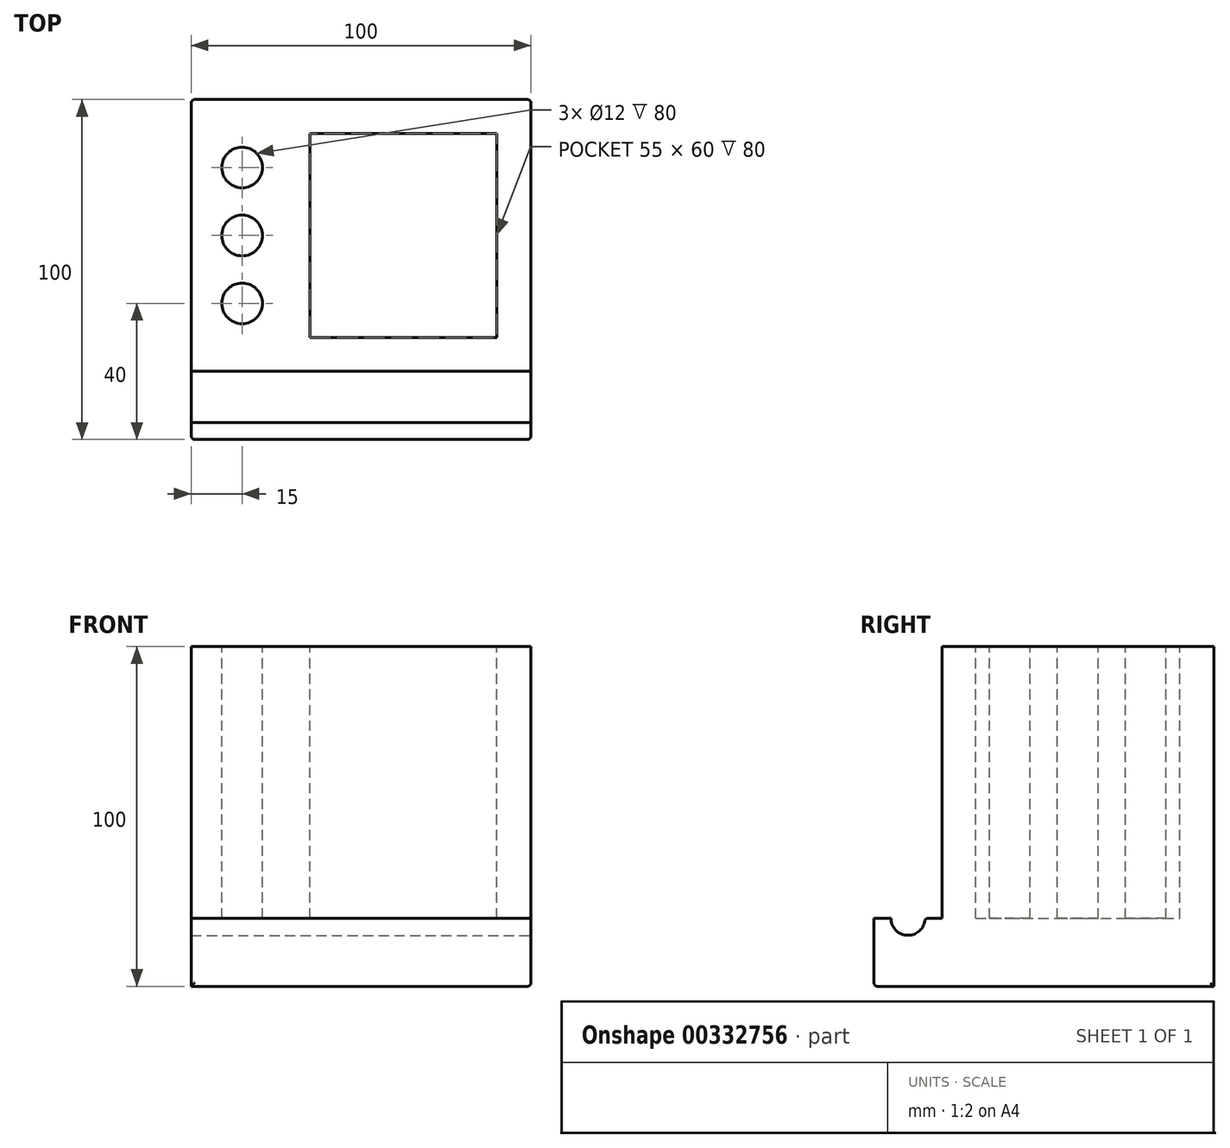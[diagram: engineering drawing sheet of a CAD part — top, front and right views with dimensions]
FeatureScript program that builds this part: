
annotation { "Feature Type Name" : "Feature", "Feature Type Description" : "" }
export const myFeature = defineFeature(function(context is Context, id is Id, definition is map)
    precondition{}
    {
        {
            var Q0;
            Q0=qCreatedBy(makeId("Top.planeOp"),FACE);
            var sketch = newSketch(context, id + "F0", { "sketchPlane" : qUnion([Q0])});
            skLineSegment(sketch, "E0.bottom", {"start": v(-50, 50) * mm, "end": v(50, 50) * mm});
            skLineSegment(sketch, "E0.top", {"start": v(-50, -50) * mm, "end": v(50, -50) * mm});
            skLineSegment(sketch, "E0.left", {"start": v(-50, 50) * mm, "end": v(-50, -50) * mm});
            skLineSegment(sketch, "E0.right", {"start": v(50, 50) * mm, "end": v(50, -50) * mm});
            skPoint(sketch, "E0.middle", {"position": v(0, 0) * mm});
            skSolve(sketch);
        }
        {
            var Q0;
            Q0 = qSketchRegion(id + "F0", true);
            extrude(context, id + "F1", {"entities" : qUnion([Q0]), "depth" : 100 * mm});
        }
        {
            var Q0;
            Q0=makeQuery(id+"F1.opExtrude","CAP_FACE",FACE,{"disambiguationData":[OSD([sQuery(id+"F0.wireOp",EDGE,"E0.bottom"),sQuery(id+"F0.wireOp",EDGE,"E0.top"),sQuery(id+"F0.wireOp",EDGE,"E0.left"),sQuery(id+"F0.wireOp",EDGE,"E0.right")])],"isStart":false});
            var sketch = newSketch(context, id + "F2", { "sketchPlane" : qUnion([Q0])});
            skLineSegment(sketch, "E1.bottom", {"start": v(-50, -30) * mm, "end": v(50, -30) * mm});
            skLineSegment(sketch, "E1.top", {"start": v(-50, -50) * mm, "end": v(50, -50) * mm});
            skLineSegment(sketch, "E1.left", {"start": v(-50, -30) * mm, "end": v(-50, -50) * mm});
            skLineSegment(sketch, "E1.right", {"start": v(50, -30) * mm, "end": v(50, -50) * mm});
            skPoint(sketch, "E1.middle", {"position": v(0, -40) * mm});
            skSolve(sketch);
        }
        {
            var Q0;
            Q0=makeQuery(id+"F2.imprint","IMPRINT",FACE,{"disambiguationData":[TD([[makeQuery(id+"F2.imprint","IMPRINT",EDGE,{"derivedFrom":sQuery(id+"F2.wireOp",EDGE,"E1.bottom")}),-1.0]])]});
            extrude(context, id + "F3", {"entities" : qUnion([Q0]), "operationType" : NewBodyOperationType.REMOVE, "oppositeDirection" : true, "depth" : 80 * mm});
        }
        {
            var Q0;
            Q0=makeQuery(id+"F1.opExtrude","CAP_FACE",FACE,{"disambiguationData":[OSD([sQuery(id+"F0.wireOp",EDGE,"E0.bottom"),sQuery(id+"F0.wireOp",EDGE,"E0.top"),sQuery(id+"F0.wireOp",EDGE,"E0.left"),sQuery(id+"F0.wireOp",EDGE,"E0.right")])],"isStart":false});
            var sketch = newSketch(context, id + "F4", { "sketchPlane" : qUnion([Q0])});
            skLineSegment(sketch, "E2.bottom", {"start": v(-15, 40) * mm, "end": v(40, 40) * mm});
            skLineSegment(sketch, "E2.top", {"start": v(-15, -20) * mm, "end": v(40, -20) * mm});
            skLineSegment(sketch, "E2.left", {"start": v(-15, 40) * mm, "end": v(-15, -20) * mm});
            skLineSegment(sketch, "E2.right", {"start": v(40, 40) * mm, "end": v(40, -20) * mm});
            skPoint(sketch, "E2.middle", {"position": v(12.5, 10) * mm});
            skLineSegment(sketch, "E3.bottom", {"start": v(-2.5, -20) * mm, "end": v(27.5, -20) * mm});
            skLineSegment(sketch, "E3.top", {"start": v(-2.5, -30) * mm, "end": v(27.5, -30) * mm});
            skLineSegment(sketch, "E3.left", {"start": v(-2.5, -20) * mm, "end": v(-2.5, -30) * mm});
            skLineSegment(sketch, "E3.right", {"start": v(27.5, -20) * mm, "end": v(27.5, -30) * mm});
            skPoint(sketch, "E3.middle", {"position": v(12.5, -25) * mm});
            skSolve(sketch);
        }
        {
            var Q0;
            Q0=makeQuery(id+"F4.imprint","IMPRINT",FACE,{"disambiguationData":[TD([[makeQuery(id+"F4.imprint","IMPRINT",EDGE,{"derivedFrom":sQuery(id+"F4.wireOp",EDGE,"E2.bottom")}),-1.0]])]});
            var Q1;
            Q1=makeQuery(id+"F4.imprint","IMPRINT",FACE,{"disambiguationData":[TD([[makeQuery(id+"F4.imprint","IMPRINT",EDGE,{"derivedFrom":sQuery(id+"F4.wireOp",EDGE,"E3.bottom")}),-1.0]])]});
            var Q2;
            Q2=makeQuery(id+"F3.boolean.opBoolean","COPY",FACE,{"derivedFrom":makeQuery(id+"F3.opExtrude","CAP_FACE",FACE,{"disambiguationData":[OSD([sQuery(id+"F2.wireOp",EDGE,"E1.bottom"),sQuery(id+"F2.wireOp",EDGE,"E1.top"),sQuery(id+"F2.wireOp",EDGE,"E1.left"),sQuery(id+"F2.wireOp",EDGE,"E1.right")])],"isStart":false})});
            extrude(context, id + "F5", {"entities" : qUnion([Q0, Q1]), "operationType" : NewBodyOperationType.REMOVE, "endBound" : BoundingType.UP_TO_SURFACE, "oppositeDirection" : true, "endBoundEntityFace" : qUnion([Q2]), "depth" : 25 * mm});
        }
        {
            var Q0;
            Q0=makeQuery(id+"F1.opExtrude","CAP_FACE",FACE,{"disambiguationData":[OSD([sQuery(id+"F0.wireOp",EDGE,"E0.bottom"),sQuery(id+"F0.wireOp",EDGE,"E0.top"),sQuery(id+"F0.wireOp",EDGE,"E0.left"),sQuery(id+"F0.wireOp",EDGE,"E0.right")])],"isStart":false});
            var sketch = newSketch(context, id + "F6", { "sketchPlane" : qUnion([Q0])});
            skCircle(sketch, "E4", {"center": v(-35, 30) * mm, "radius": 6 * mm});
            skCircle(sketch, "E5", {"center": v(-35, 10) * mm, "radius": 6 * mm});
            skCircle(sketch, "E6", {"center": v(-35, -10) * mm, "radius": 6 * mm});
            skLineSegment(sketch, "E7", {"start": v(-35, 10) * mm, "end": v(-35, 30) * mm, "construction": true});
            skLineSegment(sketch, "E8", {"start": v(-35, -10) * mm, "end": v(-35, 10) * mm, "construction": true});
            skLineSegment(sketch, "E9", {"start": v(-35, 30) * mm, "end": v(-35, 50) * mm, "construction": true});
            skLineSegment(sketch, "E10", {"start": v(-35, -10) * mm, "end": v(-35, -30) * mm, "construction": true});
            skSolve(sketch);
        }
        {
            var Q0;
            Q0=makeQuery(id+"F6.imprint","IMPRINT",FACE,{"disambiguationData":[TD([[makeQuery(id+"F6.imprint","IMPRINT",EDGE,{"derivedFrom":sQuery(id+"F6.wireOp",EDGE,"E6")}),1.0]])]});
            var Q1;
            Q1=makeQuery(id+"F6.imprint","IMPRINT",FACE,{"disambiguationData":[TD([[makeQuery(id+"F6.imprint","IMPRINT",EDGE,{"derivedFrom":sQuery(id+"F6.wireOp",EDGE,"E5")}),1.0]])]});
            var Q2;
            Q2=makeQuery(id+"F6.imprint","IMPRINT",FACE,{"disambiguationData":[TD([[makeQuery(id+"F6.imprint","IMPRINT",EDGE,{"derivedFrom":sQuery(id+"F6.wireOp",EDGE,"E4")}),1.0]])]});
            var Q3;
            Q3=makeQuery(id+"F5.boolean.opBoolean","MERGE",FACE,{"derivedFrom":[makeQuery(id+"F3.boolean.opBoolean","COPY",FACE,{"derivedFrom":makeQuery(id+"F3.opExtrude","CAP_FACE",FACE,{"disambiguationData":[OSD([sQuery(id+"F2.wireOp",EDGE,"E1.bottom"),sQuery(id+"F2.wireOp",EDGE,"E1.top"),sQuery(id+"F2.wireOp",EDGE,"E1.left"),sQuery(id+"F2.wireOp",EDGE,"E1.right")])],"isStart":false})})],"fromTools":[makeQuery(id+"F5.opExtrude","CAP_FACE",FACE,{"disambiguationData":[OSD([sQuery(id+"F4.wireOp",EDGE,"E2.bottom"),sQuery(id+"F4.wireOp",EDGE,"E2.top"),sQuery(id+"F4.wireOp",EDGE,"E2.left"),sQuery(id+"F4.wireOp",EDGE,"E2.right"),sQuery(id+"F4.wireOp",EDGE,"E3.top"),sQuery(id+"F4.wireOp",EDGE,"E3.left"),sQuery(id+"F4.wireOp",EDGE,"E3.right")])],"isStart":false})]});
            var Q4;
            Q4=makeQuery(id+"F1.opExtrude","SWEPT_BODY",BODY,{"disambiguationData":[OSD([sQuery(id+"F0.wireOp",EDGE,"E0.bottom"),sQuery(id+"F0.wireOp",EDGE,"E0.top"),sQuery(id+"F0.wireOp",EDGE,"E0.left"),sQuery(id+"F0.wireOp",EDGE,"E0.right")])]});
            extrude(context, id + "F7", {"entities" : qUnion([Q0, Q1, Q2]), "operationType" : NewBodyOperationType.REMOVE, "endBound" : BoundingType.UP_TO_SURFACE, "oppositeDirection" : true, "endBoundEntityFace" : qUnion([Q3]), "endBoundEntityBody" : qUnion([Q4]), "depth" : 25 * mm});
        }
        {
            var Q0;
            Q0=makeQuery(id+"F1.opExtrude","SWEPT_FACE",FACE,{"disambiguationData":[OSD([sQuery(id+"F0.wireOp",EDGE,"E0.right")])]});
            var sketch = newSketch(context, id + "F8", { "sketchPlane" : qUnion([Q0])});
            skCircle(sketch, "E11", {"center": v(-40, 20) * mm, "radius": 5 * mm});
            skSolve(sketch);
        }
        {
            var Q0;
            {var subQ0=sQuery(id+"F8.wireOp",EDGE,"E11");var subQ1=makeQuery(id+"F3.boolean.opBoolean","COPY",EDGE,{"derivedFrom":makeQuery(id+"F3.opExtrude","CAP_EDGE",EDGE,{"disambiguationData":[OSD([sQuery(id+"F2.wireOp",EDGE,"E1.right")])],"isStart":false})});var subQ2=makeQuery(id+"F8.imprint","INTERSECT",VERTEX,{"disambiguationData":[OD(0.0)],"derivedFrom":[subQ1,subQ0]});Q0=makeQuery(id+"F8.imprint","IMPRINT",FACE,{"disambiguationData":[TD([[makeQuery(id+"F8.imprint","IMPRINT",EDGE,{"disambiguationData":[TD([[subQ2,-1.0]])],"derivedFrom":subQ0}),1.0]])]});}
            var Q1;
            Q1=makeQuery(id+"F1.opExtrude","SWEPT_FACE",FACE,{"disambiguationData":[OSD([sQuery(id+"F0.wireOp",EDGE,"E0.left")])]});
            extrude(context, id + "F9", {"entities" : qUnion([Q0]), "operationType" : NewBodyOperationType.REMOVE, "endBound" : BoundingType.UP_TO_SURFACE, "oppositeDirection" : true, "endBoundEntityFace" : qUnion([Q1]), "depth" : 25 * mm});
        }
        {
            var Q0;
            {var subQ0=sQuery(id+"F8.wireOp",EDGE,"E11");var subQ1=sQuery(id+"F2.wireOp",EDGE,"E1.right");Q0=makeQuery(id+"F9.boolean.opBoolean","COPY",EDGE,{"derivedFrom":makeQuery(id+"F9.opExtrude","SWEPT_EDGE",EDGE,{"disambiguationData":[OSD([subQ1,subQ0]),TDD([makeQuery(id+"F8.imprint","INTERSECT",VERTEX,{"disambiguationData":[OD(1.0)],"derivedFrom":[makeQuery(id+"F3.boolean.opBoolean","COPY",EDGE,{"derivedFrom":makeQuery(id+"F3.opExtrude","CAP_EDGE",EDGE,{"disambiguationData":[OSD([subQ1])],"isStart":false})}),subQ0]})])]})});}
            var Q1;
            {var subQ0=sQuery(id+"F8.wireOp",EDGE,"E11");var subQ1=sQuery(id+"F2.wireOp",EDGE,"E1.right");Q1=makeQuery(id+"F9.boolean.opBoolean","COPY",EDGE,{"derivedFrom":makeQuery(id+"F9.opExtrude","SWEPT_EDGE",EDGE,{"disambiguationData":[OSD([subQ1,subQ0]),TDD([makeQuery(id+"F8.imprint","INTERSECT",VERTEX,{"disambiguationData":[OD(0.0)],"derivedFrom":[makeQuery(id+"F3.boolean.opBoolean","COPY",EDGE,{"derivedFrom":makeQuery(id+"F3.opExtrude","CAP_EDGE",EDGE,{"disambiguationData":[OSD([subQ1])],"isStart":false})}),subQ0]})])]})});}
            var Q2;
            Q2=makeQuery(id+"F1.opExtrude","SWEPT_EDGE",EDGE,{"disambiguationData":[OSD([sQuery(id+"F0.wireOp",EDGE,"E0.top"),sQuery(id+"F0.wireOp",EDGE,"E0.right")])]});
            var Q3;
            Q3=makeQuery(id+"F3.boolean.opBoolean","COPY",EDGE,{"derivedFrom":makeQuery(id+"F3.opExtrude","CAP_EDGE",EDGE,{"disambiguationData":[OSD([sQuery(id+"F2.wireOp",EDGE,"E1.top")])],"isStart":false})});
            var Q4;
            Q4=makeQuery(id+"F1.opExtrude","SWEPT_EDGE",EDGE,{"disambiguationData":[OSD([sQuery(id+"F0.wireOp",EDGE,"E0.top"),sQuery(id+"F0.wireOp",EDGE,"E0.left")])]});
            var Q5;
            Q5=makeQuery(id+"F1.opExtrude","CAP_EDGE",EDGE,{"disambiguationData":[OSD([sQuery(id+"F0.wireOp",EDGE,"E0.top")])],"isStart":true});
            var Q6;
            Q6=makeQuery(id+"F1.opExtrude","CAP_EDGE",EDGE,{"disambiguationData":[OSD([sQuery(id+"F0.wireOp",EDGE,"E0.right")])],"isStart":true});
            var Q7;
            Q7=makeQuery(id+"F9.boolean.opBoolean","COPY",EDGE,{"derivedFrom":makeQuery(id+"F9.opExtrude","CAP_EDGE",EDGE,{"disambiguationData":[OSD([sQuery(id+"F8.wireOp",EDGE,"E11")])],"isStart":true})});
            var Q8;
            {var subQ0=sQuery(id+"F2.wireOp",EDGE,"E1.right");Q8=makeQuery(id+"F9.boolean.opBoolean","SPLIT",EDGE,{"disambiguationData":[TD([makeQuery(id+"F1.opExtrude","SWEPT_FACE",FACE,{"disambiguationData":[OSD([sQuery(id+"F0.wireOp",EDGE,"E0.top")])]})])],"derivedFrom":makeQuery(id+"F3.boolean.opBoolean","COPY",EDGE,{"derivedFrom":makeQuery(id+"F3.opExtrude","CAP_EDGE",EDGE,{"disambiguationData":[OSD([subQ0])],"isStart":false})})});}
            var Q9;
            {var subQ0=sQuery(id+"F2.wireOp",EDGE,"E1.right");var subQ1=sQuery(id+"F2.wireOp",EDGE,"E1.bottom");Q9=makeQuery(id+"F9.boolean.opBoolean","SPLIT",EDGE,{"disambiguationData":[TD([makeQuery(id+"F3.boolean.opBoolean","COPY",FACE,{"derivedFrom":makeQuery(id+"F3.opExtrude","SWEPT_FACE",FACE,{"disambiguationData":[OSD([subQ1])]})})])],"derivedFrom":makeQuery(id+"F3.boolean.opBoolean","COPY",EDGE,{"derivedFrom":makeQuery(id+"F3.opExtrude","CAP_EDGE",EDGE,{"disambiguationData":[OSD([subQ0])],"isStart":false})})});}
            var Q10;
            Q10=makeQuery(id+"F3.boolean.opBoolean","COPY",EDGE,{"derivedFrom":makeQuery(id+"F3.opExtrude","SWEPT_EDGE",EDGE,{"disambiguationData":[OSD([sQuery(id+"F0.wireOp",EDGE,"E0.right"),sQuery(id+"F2.wireOp",EDGE,"E1.bottom"),sQuery(id+"F2.wireOp",EDGE,"E1.right")])]})});
            var Q11;
            Q11=makeQuery(id+"F9.boolean.opBoolean","COPY",EDGE,{"derivedFrom":makeQuery(id+"F9.opExtrude","CAP_EDGE",EDGE,{"disambiguationData":[OSD([sQuery(id+"F8.wireOp",EDGE,"E11")])],"isStart":false})});
            var Q12;
            {var subQ0=sQuery(id+"F2.wireOp",EDGE,"E1.left");Q12=makeQuery(id+"F9.boolean.opBoolean","SPLIT",EDGE,{"disambiguationData":[TD([makeQuery(id+"F1.opExtrude","SWEPT_FACE",FACE,{"disambiguationData":[OSD([sQuery(id+"F0.wireOp",EDGE,"E0.top")])]})])],"derivedFrom":makeQuery(id+"F3.boolean.opBoolean","COPY",EDGE,{"derivedFrom":makeQuery(id+"F3.opExtrude","CAP_EDGE",EDGE,{"disambiguationData":[OSD([subQ0])],"isStart":false})})});}
            var Q13;
            {var subQ0=sQuery(id+"F2.wireOp",EDGE,"E1.bottom");var subQ1=sQuery(id+"F2.wireOp",EDGE,"E1.left");Q13=makeQuery(id+"F9.boolean.opBoolean","SPLIT",EDGE,{"disambiguationData":[TD([makeQuery(id+"F3.boolean.opBoolean","COPY",FACE,{"derivedFrom":makeQuery(id+"F3.opExtrude","SWEPT_FACE",FACE,{"disambiguationData":[OSD([subQ0])]})})])],"derivedFrom":makeQuery(id+"F3.boolean.opBoolean","COPY",EDGE,{"derivedFrom":makeQuery(id+"F3.opExtrude","CAP_EDGE",EDGE,{"disambiguationData":[OSD([subQ1])],"isStart":false})})});}
            var Q14;
            Q14=makeQuery(id+"F1.opExtrude","SWEPT_EDGE",EDGE,{"disambiguationData":[OSD([sQuery(id+"F0.wireOp",EDGE,"E0.bottom"),sQuery(id+"F0.wireOp",EDGE,"E0.right")])]});
            var Q15;
            Q15=makeQuery(id+"F3.boolean.opBoolean","COPY",EDGE,{"derivedFrom":makeQuery(id+"F3.opExtrude","SWEPT_EDGE",EDGE,{"disambiguationData":[OSD([sQuery(id+"F0.wireOp",EDGE,"E0.left"),sQuery(id+"F2.wireOp",EDGE,"E1.bottom"),sQuery(id+"F2.wireOp",EDGE,"E1.left")])]})});
            var Q16;
            Q16=makeQuery(id+"F1.opExtrude","SWEPT_EDGE",EDGE,{"disambiguationData":[OSD([sQuery(id+"F0.wireOp",EDGE,"E0.bottom"),sQuery(id+"F0.wireOp",EDGE,"E0.left")])]});
            fillet(context, id + "F10", {"entities" : qUnion([Q0, Q1, Q2, Q3, Q4, Q5, Q6, Q7, Q8, Q9, Q10, Q11, Q12, Q13, Q14, Q15, Q16]), "radius" : 1 * mm, "tangentPropagation" : true, "allowEdgeOverflow" : false});
        }
    });
